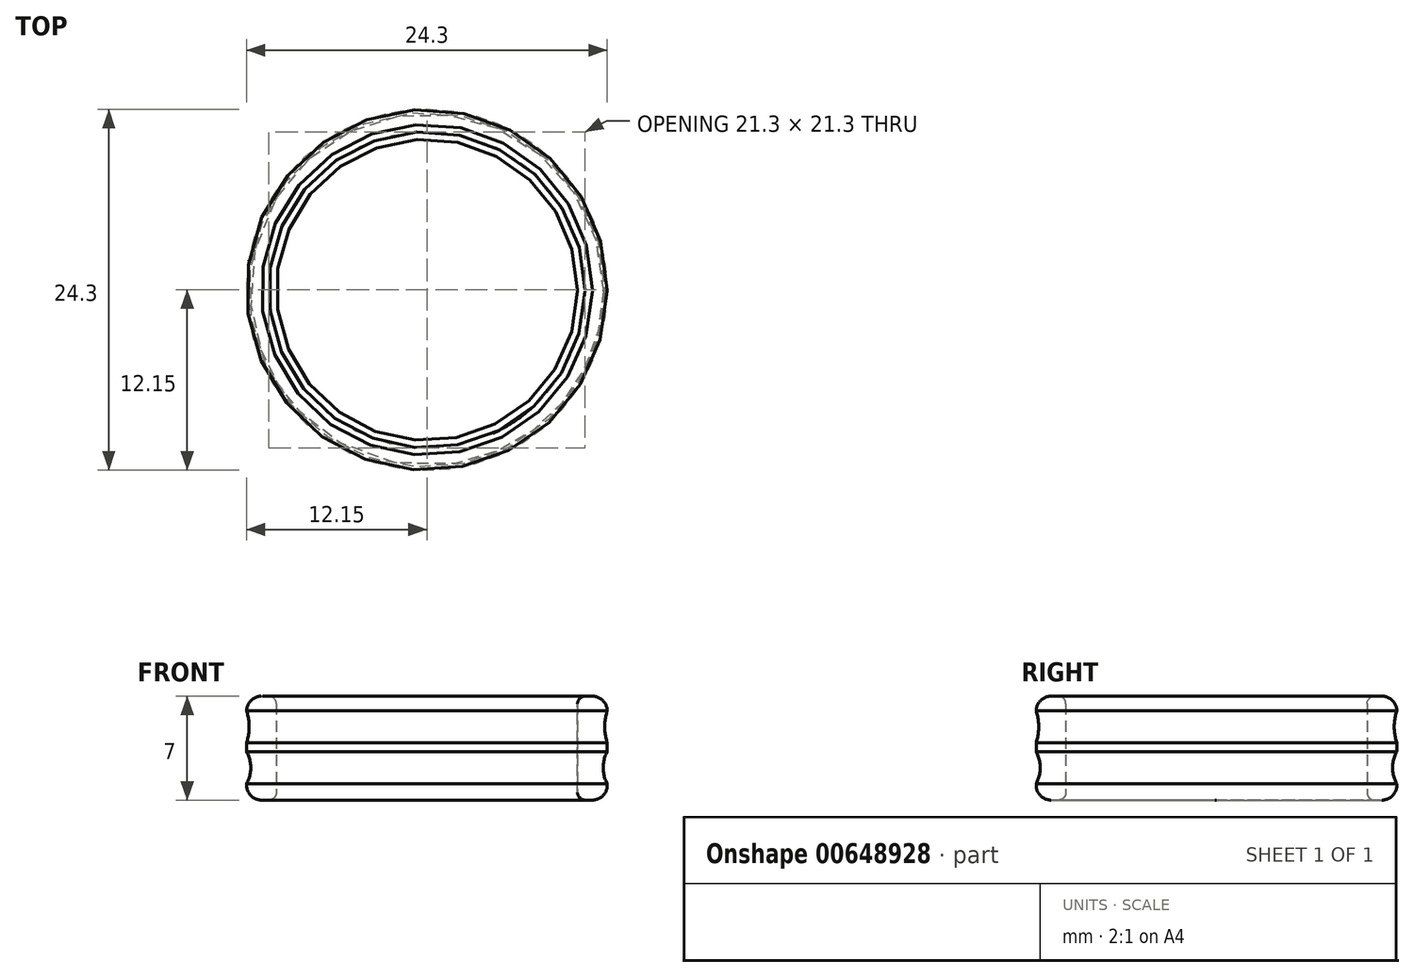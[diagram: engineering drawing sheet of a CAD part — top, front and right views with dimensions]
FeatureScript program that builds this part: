
annotation { "Feature Type Name" : "Feature", "Feature Type Description" : "" }
export const myFeature = defineFeature(function(context is Context, id is Id, definition is map)
    precondition{}
    {
        {
            var Q0;
            Q0=qCreatedBy(makeId("Front.planeOp"),FACE);
            var sketch = newSketch(context, id + "F0", { "sketchPlane" : qUnion([Q0])});
            skLineSegment(sketch, "E0", {"start": v(0, 0) * mm, "end": v(10.15, 0) * mm, "construction": true});
            skLineSegment(sketch, "E1.top", {"start": v(10.65, 3.5) * mm, "end": v(11.15, 3.5) * mm});
            skLineSegment(sketch, "E1.left", {"start": v(10.15, 0) * mm, "end": v(10.15, 3) * mm});
            skLineSegment(sketch, "E1.right", {"start": v(12.15, 0) * mm, "end": v(12.15, 2.5) * mm});
            skPoint(sketch, "E2.visualSharp", {"position": v(12.15, 3.5) * mm});
            skArc(sketch, "E2.filletArc", {"start": v(12.15, 2.5) * mm, "mid": v(11.86, 3.2) * mm, "end": v(11.15, 3.5) * mm});
            skPoint(sketch, "E3.visualSharp", {"position": v(10.15, 3.5) * mm});
            skArc(sketch, "E3.filletArc", {"start": v(10.65, 3.5) * mm, "mid": v(10.3, 3.35) * mm, "end": v(10.15, 3) * mm});
            skLineSegment(sketch, "E4.MirrorCS", {"start": v(10.65, -3.5) * mm, "end": v(11.15, -3.5) * mm});
            skArc(sketch, "E5.MirrorCS", {"start": v(10.65, -3.5) * mm, "mid": v(10.3, -3.35) * mm, "end": v(10.15, -3) * mm});
            skPoint(sketch, "E6.MirrorP", {"position": v(12.15, -3.5) * mm});
            skLineSegment(sketch, "E7.MirrorCS", {"start": v(10.15, 0) * mm, "end": v(10.15, -3) * mm});
            skArc(sketch, "E8.MirrorCS", {"start": v(12.15, -2.5) * mm, "mid": v(11.86, -3.2) * mm, "end": v(11.15, -3.5) * mm});
            skPoint(sketch, "E9.MirrorP", {"position": v(10.15, -3.5) * mm});
            skLineSegment(sketch, "E10.MirrorCS", {"start": v(12.15, 0) * mm, "end": v(12.15, -2.5) * mm});
            skPoint(sketch, "E11.MirrorCS.end.orphan", {"position": v(12.15, 0) * mm});
            skLineSegment(sketch, "E12", {"start": v(0, 0) * mm, "end": v(0, 5.63) * mm, "construction": true});
            skSolve(sketch);
        }
        {
            var Q0;
            Q0=qCreatedBy(makeId("Front.planeOp"),FACE);
            var sketch = newSketch(context, id + "F1", { "sketchPlane" : qUnion([Q0])});
            skCircle(sketch, "E13", {"center": v(15.28, 1.44) * mm, "radius": 3.3 * mm});
            skPoint(sketch, "E13.first.point", {"position": v(12.16, 2.53) * mm});
            skPoint(sketch, "E13.second.point", {"position": v(12.3, 0) * mm});
            skPoint(sketch, "E13.third.point", {"position": v(18.54, 2.06) * mm});
            skCircle(sketch, "E14", {"center": v(14.1, -1.32) * mm, "radius": 2.23 * mm});
            skPoint(sketch, "E14.first.point", {"position": v(12.18, -2.45) * mm});
            skPoint(sketch, "E14.third.point", {"position": v(16.3, -1.71) * mm});
            skSolve(sketch);
        }
        {
            var Q0;
            Q0=makeQuery(id+"F0.imprint","IMPRINT",FACE,{"disambiguationData":[TD([[makeQuery(id+"F0.imprint","IMPRINT",EDGE,{"derivedFrom":sQuery(id+"F0.wireOp",EDGE,"E1.top")}),-1.0]])]});
            var Q1;
            {var subQ0=sQuery(id+"F1.wireOp",EDGE,"E14");var subQ1=sQuery(id+"F1.wireOp",EDGE,"E13");var subQ2=makeQuery(id+"F1.imprint","INTERSECT",VERTEX,{"disambiguationData":[OD(0.0)],"derivedFrom":[subQ1,subQ0]});Q1=makeQuery(id+"F1.imprint","IMPRINT",FACE,{"disambiguationData":[TD([[makeQuery(id+"F1.imprint","IMPRINT",EDGE,{"disambiguationData":[TD([[subQ2,1.0]])],"derivedFrom":subQ1}),1.0]])]});}
            var Q2;
            {var subQ0=sQuery(id+"F1.wireOp",EDGE,"E14");var subQ1=sQuery(id+"F1.wireOp",EDGE,"E13");var subQ2=makeQuery(id+"F1.imprint","INTERSECT",VERTEX,{"disambiguationData":[OD(0.0)],"derivedFrom":[subQ1,subQ0]});Q2=makeQuery(id+"F1.imprint","IMPRINT",FACE,{"disambiguationData":[TD([[makeQuery(id+"F1.imprint","IMPRINT",EDGE,{"disambiguationData":[TD([[subQ2,-1.0]])],"derivedFrom":subQ1}),-1.0]])]});}
            extrude(context, id + "F2", {"entities" : qUnion([Q0, Q1, Q2]), "depth" : .1 * mm, "offsetDistance" : 25 * mm});
        }
        {
            var Q0;
            {var subQ0=sQuery(id+"F1.wireOp",EDGE,"E14");var subQ1=sQuery(id+"F1.wireOp",EDGE,"E13");var subQ2=makeQuery(id+"F1.imprint","INTERSECT",VERTEX,{"disambiguationData":[OD(0.0)],"derivedFrom":[subQ1,subQ0]});Q0=makeQuery(id+"F2.opExtrude","SWEPT_BODY",BODY,{"disambiguationData":[OSD([subQ1,subQ0]),TDD([makeQuery(id+"F1.imprint","IMPRINT",EDGE,{"disambiguationData":[TD([[subQ2,1.0]])],"derivedFrom":subQ1}),makeQuery(id+"F1.imprint","IMPRINT",EDGE,{"disambiguationData":[TD([[subQ2,1.0]])],"derivedFrom":subQ0})])]});}
            var Q1;
            {var subQ0=sQuery(id+"F1.wireOp",EDGE,"E14");var subQ1=sQuery(id+"F1.wireOp",EDGE,"E13");var subQ2=makeQuery(id+"F1.imprint","INTERSECT",VERTEX,{"disambiguationData":[OD(0.0)],"derivedFrom":[subQ1,subQ0]});Q1=makeQuery(id+"F2.opExtrude","SWEPT_BODY",BODY,{"disambiguationData":[OSD([subQ1,subQ0]),TDD([makeQuery(id+"F1.imprint","IMPRINT",EDGE,{"disambiguationData":[TD([[subQ2,-1.0]])],"derivedFrom":subQ1}),makeQuery(id+"F1.imprint","IMPRINT",EDGE,{"disambiguationData":[TD([[subQ2,-1.0]])],"derivedFrom":subQ0})])]});}
            var Q2;
            Q2=makeQuery(id+"F2.opExtrude","SWEPT_BODY",BODY,{"disambiguationData":[OSD([sQuery(id+"F0.wireOp",EDGE,"E1.top"),sQuery(id+"F0.wireOp",EDGE,"E1.left"),sQuery(id+"F0.wireOp",EDGE,"E1.right"),sQuery(id+"F0.wireOp",EDGE,"E2.filletArc"),sQuery(id+"F0.wireOp",EDGE,"E3.filletArc"),sQuery(id+"F0.wireOp",EDGE,"E4.MirrorCS"),sQuery(id+"F0.wireOp",EDGE,"E5.MirrorCS"),sQuery(id+"F0.wireOp",EDGE,"E7.MirrorCS"),sQuery(id+"F0.wireOp",EDGE,"E8.MirrorCS"),sQuery(id+"F0.wireOp",EDGE,"E10.MirrorCS")])]});
            booleanBodies(context, id + "F3", {"operationType" : BooleanOperationType.SUBTRACTION, "tools" : qUnion([Q0, Q1]), "targets" : qUnion([Q2])});
        }
        {
            var Q0;
            Q0=qCreatedBy(makeId("Front.planeOp"),FACE);
            var sketch = newSketch(context, id + "F4", { "sketchPlane" : qUnion([Q0])});
            skLineSegment(sketch, "E15", {"start": v(0, 0) * mm, "end": v(0, 5.05) * mm, "construction": true});
            skLineSegment(sketch, "E16", {"start": v(0, 0) * mm, "end": v(10.16, 0) * mm, "construction": true});
            skSolve(sketch);
        }
        {
            var Q0;
            Q0=makeQuery(id+"F2.opExtrude","CAP_FACE",FACE,{"disambiguationData":[OSD([sQuery(id+"F0.wireOp",EDGE,"E1.top"),sQuery(id+"F0.wireOp",EDGE,"E1.left"),sQuery(id+"F0.wireOp",EDGE,"E1.right"),sQuery(id+"F0.wireOp",EDGE,"E2.filletArc"),sQuery(id+"F0.wireOp",EDGE,"E3.filletArc"),sQuery(id+"F0.wireOp",EDGE,"E4.MirrorCS"),sQuery(id+"F0.wireOp",EDGE,"E5.MirrorCS"),sQuery(id+"F0.wireOp",EDGE,"E7.MirrorCS"),sQuery(id+"F0.wireOp",EDGE,"E8.MirrorCS"),sQuery(id+"F0.wireOp",EDGE,"E10.MirrorCS")])],"isStart":false});
            var Q1;
            Q1=sQuery(id+"F4.wireOp",EDGE,"E15");
            revolve(context, id + "F5", {"operationType" : NewBodyOperationType.ADD, "entities" : qUnion([Q0]), "axis" : qUnion([Q1]), "revolveType" : RevolveType.FULL});
        }
    });
